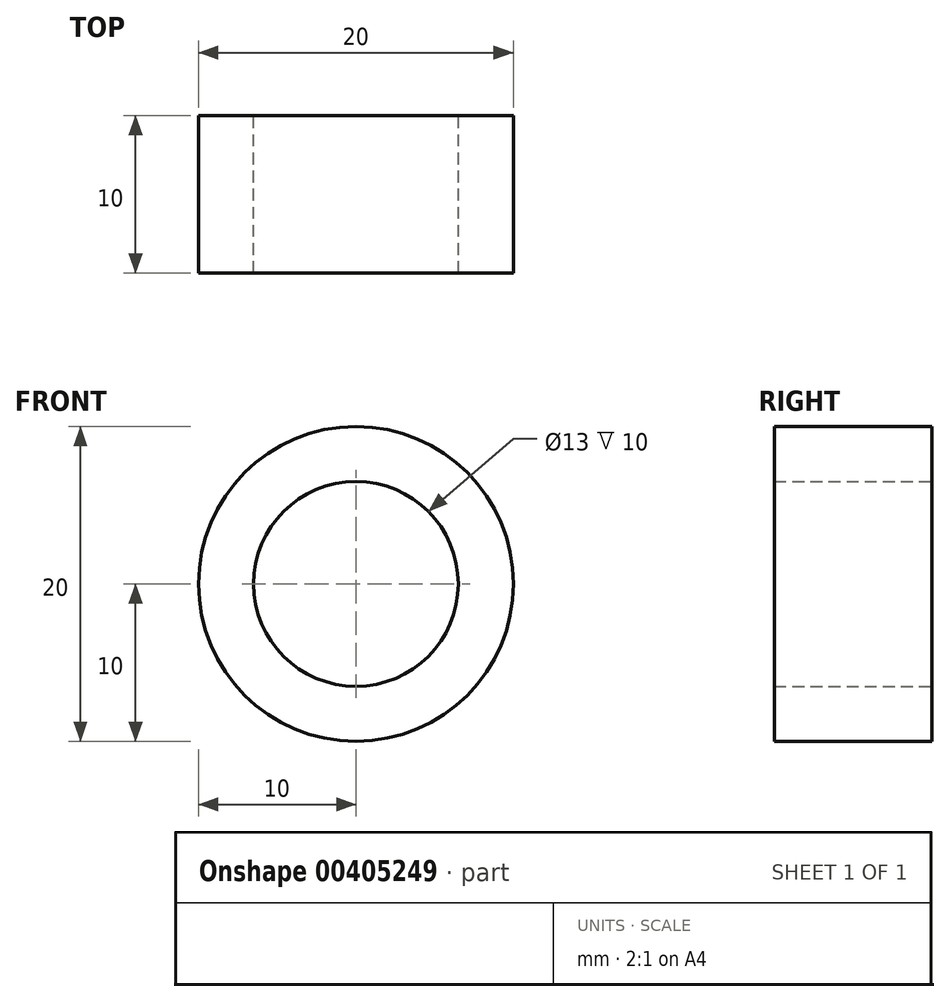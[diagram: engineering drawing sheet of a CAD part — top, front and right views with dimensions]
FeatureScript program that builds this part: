
annotation { "Feature Type Name" : "Feature", "Feature Type Description" : "" }
export const myFeature = defineFeature(function(context is Context, id is Id, definition is map)
    precondition{}
    {
        {
            var Q0;
            Q0=qCreatedBy(makeId("Front.planeOp"),FACE);
            var sketch = newSketch(context, id + "F0", { "sketchPlane" : qUnion([Q0])});
            skCircle(sketch, "E0", {"center": v(0, 0) * mm, "radius": 10 * mm});
            skCircle(sketch, "E1", {"center": v(0, 0) * mm, "radius": 6.5 * mm});
            skSolve(sketch);
        }
        {
            var Q0;
            Q0=makeQuery(id+"F0.imprint","IMPRINT",FACE,{"disambiguationData":[TD([[makeQuery(id+"F0.imprint","IMPRINT",EDGE,{"derivedFrom":sQuery(id+"F0.wireOp",EDGE,"E0")}),1.0]])]});
            extrude(context, id + "F1", {"entities" : qUnion([Q0]), "depth" : 10 * mm});
        }
    });
